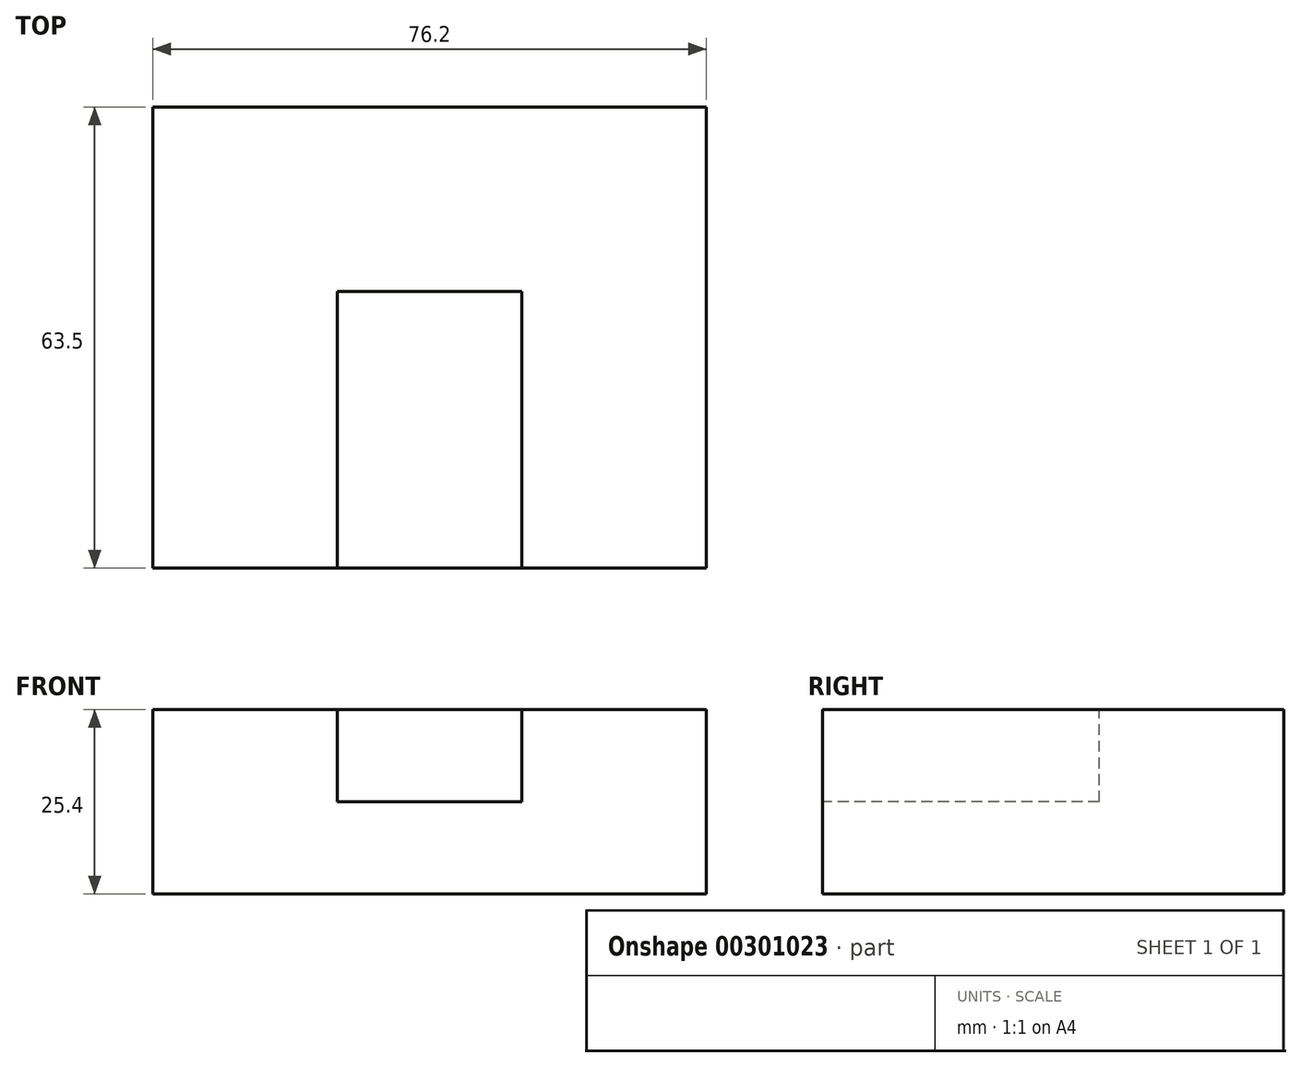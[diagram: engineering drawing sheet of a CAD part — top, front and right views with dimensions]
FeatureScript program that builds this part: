
annotation { "Feature Type Name" : "Feature", "Feature Type Description" : "" }
export const myFeature = defineFeature(function(context is Context, id is Id, definition is map)
    precondition{}
    {
        {
            var Q0;
            Q0=qCreatedBy(makeId("Front.planeOp"),FACE);
            var sketch = newSketch(context, id + "F0", { "sketchPlane" : qUnion([Q0])});
            skLineSegment(sketch, "E0.bottom", {"start": v(0, 0) * mm, "end": v(50.8, 0) * mm});
            skLineSegment(sketch, "E0.top", {"start": v(0, 12.7) * mm, "end": v(50.8, 12.7) * mm});
            skLineSegment(sketch, "E0.right", {"start": v(50.8, 0) * mm, "end": v(50.8, 12.7) * mm});
            skLineSegment(sketch, "E1.top", {"start": v(0, 12.7) * mm, "end": v(-25.4, 12.7) * mm});
            skLineSegment(sketch, "E1.right", {"start": v(-25.4, 0) * mm, "end": v(-25.4, 12.7) * mm});
            skLineSegment(sketch, "E2.top", {"start": v(-25.4, -12.7) * mm, "end": v(50.8, -12.7) * mm});
            skLineSegment(sketch, "E2.left", {"start": v(-25.4, 0) * mm, "end": v(-25.4, -12.7) * mm});
            skLineSegment(sketch, "E2.right", {"start": v(50.8, 0) * mm, "end": v(50.8, -12.7) * mm});
            skSolve(sketch);
        }
        {
            var Q0;
            Q0=makeQuery(id+"F0.imprint","IMPRINT",FACE,{"disambiguationData":[TD([[makeQuery(id+"F0.imprint","IMPRINT",EDGE,{"derivedFrom":sQuery(id+"F0.wireOp",EDGE,"E0.top")}),-1.0]])]});
            extrude(context, id + "F1", {"entities" : qUnion([Q0]), "oppositeDirection" : true, "depth" : 63.5 * mm});
        }
        {
            var Q0;
            Q0=makeQuery(id+"F1.opExtrude","CAP_FACE",FACE,{"disambiguationData":[OSD([sQuery(id+"F0.wireOp",EDGE,"E0.top"),sQuery(id+"F0.wireOp",EDGE,"E0.right"),sQuery(id+"F0.wireOp",EDGE,"E1.top"),sQuery(id+"F0.wireOp",EDGE,"E1.right"),sQuery(id+"F0.wireOp",EDGE,"E2.top"),sQuery(id+"F0.wireOp",EDGE,"E2.left"),sQuery(id+"F0.wireOp",EDGE,"E2.right")])],"isStart":true});
            var sketch = newSketch(context, id + "F2", { "sketchPlane" : qUnion([Q0])});
            skLineSegment(sketch, "E3.bottom", {"start": v(0, 0) * mm, "end": v(25.4, 0) * mm});
            skLineSegment(sketch, "E3.top", {"start": v(0, 12.7) * mm, "end": v(25.4, 12.7) * mm});
            skLineSegment(sketch, "E3.left", {"start": v(0, 0) * mm, "end": v(0, 12.7) * mm});
            skLineSegment(sketch, "E3.right", {"start": v(25.4, 0) * mm, "end": v(25.4, 12.7) * mm});
            skSolve(sketch);
        }
        {
            var Q0;
            Q0=makeQuery(id+"F2.imprint","IMPRINT",FACE,{"disambiguationData":[TD([[makeQuery(id+"F2.imprint","IMPRINT",EDGE,{"derivedFrom":sQuery(id+"F2.wireOp",EDGE,"E3.bottom")}),1.0]])]});
            extrude(context, id + "F3", {"entities" : qUnion([Q0]), "operationType" : NewBodyOperationType.REMOVE, "oppositeDirection" : true, "depth" : 38.1 * mm});
        }
    });
